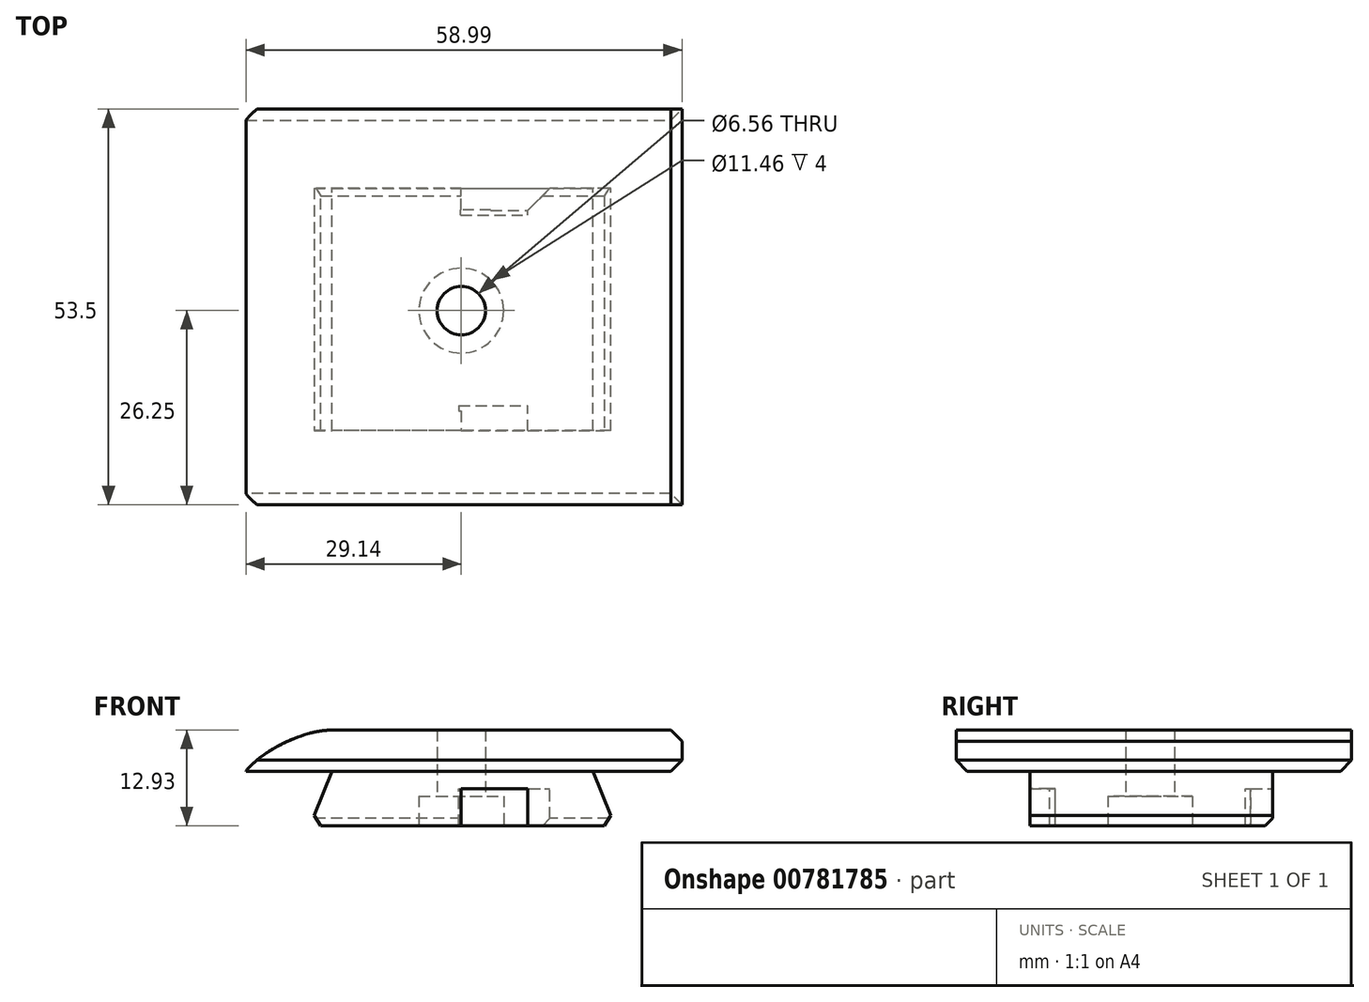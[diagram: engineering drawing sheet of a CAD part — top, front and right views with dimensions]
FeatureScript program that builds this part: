
annotation { "Feature Type Name" : "Feature", "Feature Type Description" : "" }
export const myFeature = defineFeature(function(context is Context, id is Id, definition is map)
    precondition{}
    {
        {
            var Q0;
            Q0=qCreatedBy(makeId("Front.planeOp"),FACE);
            var sketch = newSketch(context, id + "F0", { "sketchPlane" : qUnion([Q0])});
            skLineSegment(sketch, "E0", {"start": v(-49.44, 13.06) * mm, "end": v(-14.15, 13.06) * mm});
            skLineSegment(sketch, "E1", {"start": v(-14.15, 5.69) * mm, "end": v(-11.15, 5.69) * mm});
            skLineSegment(sketch, "E2", {"start": v(-11.15, 5.69) * mm, "end": v(-14.15, 13.06) * mm});
            skLineSegment(sketch, "E3", {"start": v(-49.44, 5.69) * mm, "end": v(-52.44, 5.69) * mm});
            skLineSegment(sketch, "E4", {"start": v(-52.44, 5.69) * mm, "end": v(-49.44, 13.06) * mm});
            skLineSegment(sketch, "E5", {"start": v(-49.44, 5.69) * mm, "end": v(-27.95, 5.69) * mm});
            skLineSegment(sketch, "E6", {"start": v(-27.95, 5.69) * mm, "end": v(-27.95, 10.69) * mm});
            skLineSegment(sketch, "E7", {"start": v(-27.95, 10.69) * mm, "end": v(-22.95, 10.69) * mm});
            skLineSegment(sketch, "E8", {"start": v(-22.95, 10.69) * mm, "end": v(-22.95, 5.69) * mm});
            skLineSegment(sketch, "E9", {"start": v(-22.95, 5.69) * mm, "end": v(-14.15, 5.69) * mm});
            skSolve(sketch);
        }
        {
            var Q0;
            Q0=makeQuery(id+"F0.imprint","IMPRINT",FACE,{"disambiguationData":[TD([[makeQuery(id+"F0.imprint","IMPRINT",EDGE,{"derivedFrom":sQuery(id+"F0.wireOp",EDGE,"E0")}),-1.0]])]});
            extrude(context, id + "F1", {"entities" : qUnion([Q0]), "depth" : 33.1 * mm, "offsetDistance" : 25 * mm});
        }
        {
            var Q0;
            Q0=makeQuery(id+"F1.opExtrude","SWEPT_FACE",FACE,{"disambiguationData":[OSD([sQuery(id+"F0.wireOp",EDGE,"E3"),sQuery(id+"F0.wireOp",EDGE,"E5")])]});
            var sketch = newSketch(context, id + "F2", { "sketchPlane" : qUnion([Q0])});
            skLineSegment(sketch, "E10", {"start": v(-27.95, 30.12) * mm, "end": v(-22.95, 30.12) * mm});
            skLineSegment(sketch, "E11", {"start": v(-27.95, 30.12) * mm, "end": v(-27.95, 2.97) * mm});
            skLineSegment(sketch, "E12", {"start": v(-27.95, 2.97) * mm, "end": v(-22.95, 2.97) * mm});
            skLineSegment(sketch, "E13", {"start": v(-22.95, 30.12) * mm, "end": v(-22.95, 2.97) * mm});
            skSolve(sketch);
        }
        {
            var Q0;
            Q0=makeQuery(id+"F2.imprint","IMPRINT",FACE,{"disambiguationData":[TD([[makeQuery(id+"F2.imprint","IMPRINT",EDGE,{"derivedFrom":sQuery(id+"F2.wireOp",EDGE,"E10")}),-1.0]])]});
            extrude(context, id + "F3", {"entities" : qUnion([Q0]), "oppositeDirection" : true, "depth" : 5 * mm, "offsetDistance" : 25 * mm});
        }
        {
            var Q0;
            Q0=makeQuery(id+"F1.opExtrude","SWEPT_FACE",FACE,{"disambiguationData":[OSD([sQuery(id+"F0.wireOp",EDGE,"E0")])]});
            var sketch = newSketch(context, id + "F4", { "sketchPlane" : qUnion([Q0])});
            skLineSegment(sketch, "E14", {"start": v(-49.44, -16.55) * mm, "end": v(-49.44, -33.1) * mm});
            skCircle(sketch, "E15", {"center": v(-31.95, -16.55) * mm, "radius": 5 * mm});
            skPoint(sketch, "E16.orphan", {"position": v(-31.95, 0) * mm});
            skPoint(sketch, "E17.orphan", {"position": v(-49.44, 0) * mm});
            skPoint(sketch, "E18.end.orphan", {"position": v(-31.95, -33.1) * mm});
            skSolve(sketch);
        }
        {
            var Q0;
            Q0=makeQuery(id+"F4.imprint","IMPRINT",FACE,{"disambiguationData":[TD([[makeQuery(id+"F4.imprint","IMPRINT",EDGE,{"derivedFrom":sQuery(id+"F4.wireOp",EDGE,"E15")}),1.0]])]});
            extrude(context, id + "F5", {"entities" : qUnion([Q0]), "operationType" : NewBodyOperationType.REMOVE, "oppositeDirection" : true, "depth" : 25 * mm, "offsetDistance" : 25 * mm});
        }
        {
            var Q0;
            Q0=makeQuery(id+"F3.opExtrude","CAP_FACE",FACE,{"disambiguationData":[OSD([sQuery(id+"F2.wireOp",EDGE,"E10"),sQuery(id+"F2.wireOp",EDGE,"E11"),sQuery(id+"F2.wireOp",EDGE,"E12"),sQuery(id+"F2.wireOp",EDGE,"E13")])],"isStart":true});
            var sketch = newSketch(context, id + "F6", { "sketchPlane" : qUnion([Q0])});
            skArc(sketch, "E19", {"start": v(-27.95, 13.55) * mm, "mid": v(-26.95, 16.55) * mm, "end": v(-27.95, 19.55) * mm});
            skLineSegment(sketch, "E20", {"start": v(-27.95, 19.55) * mm, "end": v(-27.95, 13.55) * mm});
            skSolve(sketch);
        }
        {
            var Q0;
            Q0=makeQuery(id+"F6.imprint","IMPRINT",FACE,{"disambiguationData":[TD([[makeQuery(id+"F6.imprint","IMPRINT",EDGE,{"derivedFrom":sQuery(id+"F6.wireOp",EDGE,"E19")}),1.0]])]});
            extrude(context, id + "F7", {"entities" : qUnion([Q0]), "operationType" : NewBodyOperationType.REMOVE, "oppositeDirection" : true, "depth" : 25 * mm, "offsetDistance" : 25 * mm});
        }
        {
            var Q0;
            Q0=makeQuery(id+"F1.opExtrude","CAP_FACE",FACE,{"disambiguationData":[OSD([sQuery(id+"F0.wireOp",EDGE,"E0"),sQuery(id+"F0.wireOp",EDGE,"E1"),sQuery(id+"F0.wireOp",EDGE,"E2"),sQuery(id+"F0.wireOp",EDGE,"E3"),sQuery(id+"F0.wireOp",EDGE,"E4"),sQuery(id+"F0.wireOp",EDGE,"E5"),sQuery(id+"F0.wireOp",EDGE,"E6"),sQuery(id+"F0.wireOp",EDGE,"E7"),sQuery(id+"F0.wireOp",EDGE,"E8"),sQuery(id+"F0.wireOp",EDGE,"E9")])],"isStart":false});
            var sketch = newSketch(context, id + "F8", { "sketchPlane" : qUnion([Q0])});
            skLineSegment(sketch, "E21", {"start": v(-52.44, 5.69) * mm, "end": v(-27.95, 5.69) * mm});
            skLineSegment(sketch, "E22", {"start": v(-27.95, 5.69) * mm, "end": v(-27.95, 10.69) * mm});
            skLineSegment(sketch, "E23", {"start": v(-27.95, 10.69) * mm, "end": v(-22.95, 10.69) * mm});
            skLineSegment(sketch, "E24", {"start": v(-22.95, 10.69) * mm, "end": v(-22.95, 5.69) * mm});
            skLineSegment(sketch, "E25", {"start": v(-22.95, 5.69) * mm, "end": v(-11.15, 5.69) * mm});
            skLineSegment(sketch, "E26", {"start": v(-11.15, 5.69) * mm, "end": v(-14.15, 13.06) * mm});
            skLineSegment(sketch, "E27", {"start": v(-14.15, 13.06) * mm, "end": v(-49.44, 13.06) * mm});
            skLineSegment(sketch, "E28", {"start": v(-49.44, 13.06) * mm, "end": v(-52.44, 5.69) * mm});
            skSolve(sketch);
        }
        {
            var Q0;
            Q0=makeQuery(id+"F8.imprint","IMPRINT",FACE,{"disambiguationData":[TD([[makeQuery(id+"F8.imprint","IMPRINT",EDGE,{"derivedFrom":sQuery(id+"F8.wireOp",EDGE,"E21")}),-1.0]])]});
            extrude(context, id + "F9", {"entities" : qUnion([Q0]), "operationType" : NewBodyOperationType.REMOVE, "oppositeDirection" : true, "depth" : .3 * mm, "offsetDistance" : 25 * mm});
        }
        {
            var Q0;
            Q0=makeQuery(id+"F9.boolean.opBoolean","COPY",FACE,{"derivedFrom":makeQuery(id+"F9.opExtrude","CAP_FACE",FACE,{"disambiguationData":[OSD([sQuery(id+"F8.wireOp",EDGE,"E21"),sQuery(id+"F8.wireOp",EDGE,"E22"),sQuery(id+"F8.wireOp",EDGE,"E23"),sQuery(id+"F8.wireOp",EDGE,"E24"),sQuery(id+"F8.wireOp",EDGE,"E25"),sQuery(id+"F8.wireOp",EDGE,"E26"),sQuery(id+"F8.wireOp",EDGE,"E27"),sQuery(id+"F8.wireOp",EDGE,"E28")])],"isStart":false})});
            var sketch = newSketch(context, id + "F10", { "sketchPlane" : qUnion([Q0])});
            skLineSegment(sketch, "E29.bottom", {"start": v(-31.95, 5.69) * mm, "end": v(-22.95, 5.69) * mm});
            skLineSegment(sketch, "E29.top", {"start": v(-31.95, 10.69) * mm, "end": v(-22.95, 10.69) * mm});
            skLineSegment(sketch, "E29.left", {"start": v(-31.95, 5.69) * mm, "end": v(-31.95, 10.69) * mm});
            skLineSegment(sketch, "E29.right", {"start": v(-22.95, 5.69) * mm, "end": v(-22.95, 10.69) * mm});
            skSolve(sketch);
        }
        {
            var Q0;
            {var subQ2=sQuery(id+"F10.wireOp",EDGE,"E29.left");Q0=makeQuery(id+"F10.imprint","IMPRINT",FACE,{"disambiguationData":[TD([[makeQuery(id+"F10.imprint","IMPRINT",EDGE,{"derivedFrom":subQ2}),-1.0]])]});}
            extrude(context, id + "F11", {"entities" : qUnion([Q0]), "operationType" : NewBodyOperationType.REMOVE, "oppositeDirection" : true, "depth" : 2.66 * mm, "offsetDistance" : 25 * mm});
        }
        {
            var Q0;
            Q0=makeQuery(id+"F1.opExtrude","CAP_FACE",FACE,{"disambiguationData":[OSD([sQuery(id+"F0.wireOp",EDGE,"E0"),sQuery(id+"F0.wireOp",EDGE,"E1"),sQuery(id+"F0.wireOp",EDGE,"E2"),sQuery(id+"F0.wireOp",EDGE,"E3"),sQuery(id+"F0.wireOp",EDGE,"E4"),sQuery(id+"F0.wireOp",EDGE,"E5"),sQuery(id+"F0.wireOp",EDGE,"E6"),sQuery(id+"F0.wireOp",EDGE,"E7"),sQuery(id+"F0.wireOp",EDGE,"E8"),sQuery(id+"F0.wireOp",EDGE,"E9")])],"isStart":true});
            var sketch = newSketch(context, id + "F12", { "sketchPlane" : qUnion([Q0])});
            skLineSegment(sketch, "E30.bottom", {"start": v(22.95, 5.69) * mm, "end": v(31.95, 5.69) * mm});
            skLineSegment(sketch, "E30.top", {"start": v(22.95, 10.69) * mm, "end": v(31.95, 10.69) * mm});
            skLineSegment(sketch, "E30.left", {"start": v(22.95, 5.69) * mm, "end": v(22.95, 10.69) * mm});
            skLineSegment(sketch, "E30.right", {"start": v(31.95, 5.69) * mm, "end": v(31.95, 10.69) * mm});
            skSolve(sketch);
        }
        {
            var Q0;
            {var subQ2=sQuery(id+"F12.wireOp",EDGE,"E30.right");Q0=makeQuery(id+"F12.imprint","IMPRINT",FACE,{"disambiguationData":[TD([[makeQuery(id+"F12.imprint","IMPRINT",EDGE,{"derivedFrom":subQ2}),1.0]])]});}
            extrude(context, id + "F13", {"entities" : qUnion([Q0]), "operationType" : NewBodyOperationType.REMOVE, "oppositeDirection" : true, "depth" : 2.91 * mm, "offsetDistance" : 25 * mm});
        }
        {
            var Q0;
            Q0=makeQuery(id+"F1.opExtrude","SWEPT_EDGE",EDGE,{"disambiguationData":[OSD([sQuery(id+"F0.wireOp",EDGE,"E1"),sQuery(id+"F0.wireOp",EDGE,"E2")])]});
            var Q1;
            Q1=makeQuery(id+"F1.opExtrude","CAP_EDGE",EDGE,{"disambiguationData":[OSD([sQuery(id+"F0.wireOp",EDGE,"E1"),sQuery(id+"F0.wireOp",EDGE,"E9")])],"isStart":true});
            var Q2;
            Q2=makeQuery(id+"F1.opExtrude","CAP_EDGE",EDGE,{"disambiguationData":[OSD([sQuery(id+"F0.wireOp",EDGE,"E3"),sQuery(id+"F0.wireOp",EDGE,"E5")])],"isStart":true});
            var Q3;
            Q3=makeQuery(id+"F1.opExtrude","SWEPT_EDGE",EDGE,{"disambiguationData":[OSD([sQuery(id+"F0.wireOp",EDGE,"E3"),sQuery(id+"F0.wireOp",EDGE,"E4")])]});
            var Q4;
            Q4=makeQuery(id+"F9.boolean.opBoolean","COPY",EDGE,{"derivedFrom":makeQuery(id+"F9.opExtrude","CAP_EDGE",EDGE,{"disambiguationData":[OSD([sQuery(id+"F8.wireOp",EDGE,"E21")])],"isStart":false})});
            var Q5;
            Q5=makeQuery(id+"F9.boolean.opBoolean","COPY",EDGE,{"derivedFrom":makeQuery(id+"F9.opExtrude","CAP_EDGE",EDGE,{"disambiguationData":[OSD([sQuery(id+"F8.wireOp",EDGE,"E25")])],"isStart":false})});
            chamfer(context, id + "F14", {"entities" : qUnion([Q0, Q1, Q2, Q3, Q4, Q5]), "width" : 1 * mm, "tangentPropagation" : true});
        }
        {
            var Q0;
            Q0=makeQuery(id+"F11.boolean.opBoolean","COPY",EDGE,{"derivedFrom":makeQuery(id+"F11.opExtrude","CAP_EDGE",EDGE,{"disambiguationData":[OSD([sQuery(id+"F10.wireOp",EDGE,"E29.left")])],"isStart":true})});
            var Q1;
            Q1=makeQuery(id+"F9.boolean.opBoolean","COPY",EDGE,{"derivedFrom":makeQuery(id+"F9.opExtrude","CAP_EDGE",EDGE,{"disambiguationData":[OSD([sQuery(id+"F8.wireOp",EDGE,"E24")])],"isStart":false})});
            var Q2;
            Q2=makeQuery(id+"F13.boolean.opBoolean","COPY",EDGE,{"derivedFrom":makeQuery(id+"F13.opExtrude","CAP_EDGE",EDGE,{"disambiguationData":[OSD([sQuery(id+"F12.wireOp",EDGE,"E30.right")])],"isStart":true})});
            var Q3;
            Q3=makeQuery(id+"F1.opExtrude","CAP_EDGE",EDGE,{"disambiguationData":[OSD([sQuery(id+"F0.wireOp",EDGE,"E8")])],"isStart":true});
            chamfer(context, id + "F15", {"entities" : qUnion([Q0, Q1, Q2, Q3]), "width" : 3 * mm, "tangentPropagation" : true});
        }
        {
            var Q0;
            Q0=makeQuery(id+"F11.boolean.opBoolean","COPY",FACE,{"derivedFrom":makeQuery(id+"F11.opExtrude","CAP_FACE",FACE,{"disambiguationData":[OSD([sQuery(id+"F8.wireOp",EDGE,"E22"),sQuery(id+"F10.wireOp",EDGE,"E29.bottom"),sQuery(id+"F10.wireOp",EDGE,"E29.top"),sQuery(id+"F10.wireOp",EDGE,"E29.left")])],"isStart":false})});
            var sketch = newSketch(context, id + "F16", { "sketchPlane" : qUnion([Q0])});
            skLineSegment(sketch, "E31.bottom", {"start": v(-32.3, 5.69) * mm, "end": v(-22.96, 5.69) * mm});
            skLineSegment(sketch, "E31.top", {"start": v(-32.3, 10.69) * mm, "end": v(-22.96, 10.69) * mm});
            skLineSegment(sketch, "E31.left", {"start": v(-32.3, 5.69) * mm, "end": v(-32.3, 10.69) * mm});
            skLineSegment(sketch, "E31.right", {"start": v(-22.96, 5.69) * mm, "end": v(-22.96, 10.69) * mm});
            skSolve(sketch);
        }
        {
            var Q0;
            Q0 = qSketchRegion(id + "F16", true);
            extrude(context, id + "F17", {"entities" : qUnion([Q0]), "operationType" : NewBodyOperationType.REMOVE, "oppositeDirection" : true, "depth" : .75 * mm, "offsetDistance" : 25 * mm});
        }
        {
            var Q0;
            Q0=makeQuery(id+"F1.opExtrude","SWEPT_BODY",BODY,{"disambiguationData":[OSD([sQuery(id+"F0.wireOp",EDGE,"E0"),sQuery(id+"F0.wireOp",EDGE,"E1"),sQuery(id+"F0.wireOp",EDGE,"E2"),sQuery(id+"F0.wireOp",EDGE,"E3"),sQuery(id+"F0.wireOp",EDGE,"E4"),sQuery(id+"F0.wireOp",EDGE,"E5"),sQuery(id+"F0.wireOp",EDGE,"E6"),sQuery(id+"F0.wireOp",EDGE,"E7"),sQuery(id+"F0.wireOp",EDGE,"E8"),sQuery(id+"F0.wireOp",EDGE,"E9")])]});
            var Q1;
            Q1=makeQuery(id+"F3.opExtrude","SWEPT_BODY",BODY,{"disambiguationData":[OSD([sQuery(id+"F2.wireOp",EDGE,"E10"),sQuery(id+"F2.wireOp",EDGE,"E11"),sQuery(id+"F2.wireOp",EDGE,"E12"),sQuery(id+"F2.wireOp",EDGE,"E13")])]});
            booleanBodies(context, id + "F18", {"operationType" : BooleanOperationType.UNION, "tools" : qUnion([Q0, Q1])});
        }
        {
            var Q0;
            Q0=makeQuery(id+"F3.opExtrude","SWEPT_FACE",FACE,{"disambiguationData":[OSD([sQuery(id+"F2.wireOp",EDGE,"E10")])]});
            var sketch = newSketch(context, id + "F19", { "sketchPlane" : qUnion([Q0])});
            skLineSegment(sketch, "E32.bottom", {"start": v(-27.95, 5.69) * mm, "end": v(-22.95, 5.69) * mm});
            skLineSegment(sketch, "E32.top", {"start": v(-27.95, 10.69) * mm, "end": v(-22.95, 10.69) * mm});
            skLineSegment(sketch, "E32.left", {"start": v(-27.95, 5.69) * mm, "end": v(-27.95, 10.69) * mm});
            skLineSegment(sketch, "E32.right", {"start": v(-22.95, 5.69) * mm, "end": v(-22.95, 10.69) * mm});
            skSolve(sketch);
        }
        {
            var Q0;
            Q0 = qSketchRegion(id + "F19", true);
            extrude(context, id + "F20", {"entities" : qUnion([Q0]), "operationType" : NewBodyOperationType.REMOVE, "oppositeDirection" : true, "depth" : .7 * mm, "offsetDistance" : 25 * mm});
        }
        {
            var Q0;
            Q0=makeQuery(id+"F13.boolean.opBoolean","COPY",FACE,{"derivedFrom":makeQuery(id+"F13.opExtrude","CAP_FACE",FACE,{"disambiguationData":[OSD([sQuery(id+"F0.wireOp",EDGE,"E6"),sQuery(id+"F12.wireOp",EDGE,"E30.bottom"),sQuery(id+"F12.wireOp",EDGE,"E30.top"),sQuery(id+"F12.wireOp",EDGE,"E30.right")])],"isStart":false})});
            var sketch = newSketch(context, id + "F21", { "sketchPlane" : qUnion([Q0])});
            skLineSegment(sketch, "E33.bottom", {"start": v(32.04, 5.69) * mm, "end": v(22.95, 5.69) * mm});
            skLineSegment(sketch, "E33.top", {"start": v(32.04, 10.66) * mm, "end": v(22.95, 10.66) * mm});
            skLineSegment(sketch, "E33.left", {"start": v(32.04, 5.69) * mm, "end": v(32.04, 10.66) * mm});
            skLineSegment(sketch, "E33.right", {"start": v(22.95, 5.69) * mm, "end": v(22.95, 10.66) * mm});
            skSolve(sketch);
        }
        {
            var Q0;
            Q0 = qSketchRegion(id + "F21", true);
            extrude(context, id + "F22", {"entities" : qUnion([Q0]), "operationType" : NewBodyOperationType.REMOVE, "oppositeDirection" : true, "depth" : .75 * mm, "offsetDistance" : 25 * mm});
        }
        {
            var Q0;
            Q0=makeQuery(id+"F9.boolean.opBoolean","COPY",FACE,{"derivedFrom":makeQuery(id+"F9.opExtrude","CAP_FACE",FACE,{"disambiguationData":[OSD([sQuery(id+"F8.wireOp",EDGE,"E21"),sQuery(id+"F8.wireOp",EDGE,"E22"),sQuery(id+"F8.wireOp",EDGE,"E23"),sQuery(id+"F8.wireOp",EDGE,"E24"),sQuery(id+"F8.wireOp",EDGE,"E25"),sQuery(id+"F8.wireOp",EDGE,"E26"),sQuery(id+"F8.wireOp",EDGE,"E27"),sQuery(id+"F8.wireOp",EDGE,"E28")])],"isStart":false})});
            var sketch = newSketch(context, id + "F23", { "sketchPlane" : qUnion([Q0])});
            skLineSegment(sketch, "E34", {"start": v(-49.44, 13.06) * mm, "end": v(-61.09, 13.06) * mm});
            skLineSegment(sketch, "E35", {"start": v(-61.09, 13.06) * mm, "end": v(-61.09, 18.62) * mm});
            skLineSegment(sketch, "E36", {"start": v(-14.15, 13.06) * mm, "end": v(-2.1, 13.06) * mm});
            skLineSegment(sketch, "E37", {"start": v(-2.1, 13.06) * mm, "end": v(-2.1, 18.62) * mm});
            skLineSegment(sketch, "E38", {"start": v(-2.1, 18.62) * mm, "end": v(-61.09, 18.62) * mm});
            skSolve(sketch);
        }
        {
            var Q0;
            Q0=makeQuery(id+"F23.imprint","IMPRINT",FACE,{"disambiguationData":[TD([[makeQuery(id+"F23.imprint","IMPRINT",EDGE,{"derivedFrom":sQuery(id+"F23.wireOp",EDGE,"E34")}),-1.0]])]});
            extrude(context, id + "F24", {"entities" : qUnion([Q0]), "operationType" : NewBodyOperationType.ADD, "oppositeDirection" : true, "depth" : 43.5 * mm, "offsetDistance" : 25 * mm});
        }
        {
            var Q0;
            {var subQ0=sQuery(id+"F8.wireOp",EDGE,"E27");Q0=makeQuery(id+"F24.boolean.opBoolean","MERGE",FACE,{"derivedFrom":[makeQuery(id+"F9.boolean.opBoolean","COPY",FACE,{"derivedFrom":makeQuery(id+"F9.opExtrude","CAP_FACE",FACE,{"disambiguationData":[OSD([sQuery(id+"F8.wireOp",EDGE,"E21"),sQuery(id+"F8.wireOp",EDGE,"E22"),sQuery(id+"F8.wireOp",EDGE,"E23"),sQuery(id+"F8.wireOp",EDGE,"E24"),sQuery(id+"F8.wireOp",EDGE,"E25"),sQuery(id+"F8.wireOp",EDGE,"E26"),subQ0,sQuery(id+"F8.wireOp",EDGE,"E28")])],"isStart":false})}),makeQuery(id+"F24.opExtrude","CAP_FACE",FACE,{"disambiguationData":[OSD([subQ0,sQuery(id+"F23.wireOp",EDGE,"E34"),sQuery(id+"F23.wireOp",EDGE,"E35"),sQuery(id+"F23.wireOp",EDGE,"E36"),sQuery(id+"F23.wireOp",EDGE,"E37"),sQuery(id+"F23.wireOp",EDGE,"E38")])],"isStart":true})]});}
            var sketch = newSketch(context, id + "F25", { "sketchPlane" : qUnion([Q0])});
            skLineSegment(sketch, "E39.bottom", {"start": v(-61.09, 18.62) * mm, "end": v(-2.1, 18.62) * mm});
            skLineSegment(sketch, "E39.top", {"start": v(-61.09, 13.06) * mm, "end": v(-2.1, 13.06) * mm});
            skLineSegment(sketch, "E39.left", {"start": v(-61.09, 18.62) * mm, "end": v(-61.09, 13.06) * mm});
            skLineSegment(sketch, "E39.right", {"start": v(-2.1, 18.62) * mm, "end": v(-2.1, 13.06) * mm});
            skSolve(sketch);
        }
        {
            var Q0;
            Q0=makeQuery(id+"F25.imprint","IMPRINT",FACE,{"disambiguationData":[TD([[makeQuery(id+"F25.imprint","IMPRINT",EDGE,{"derivedFrom":sQuery(id+"F25.wireOp",EDGE,"E39.bottom")}),1.0]])]});
            extrude(context, id + "F26", {"entities" : qUnion([Q0]), "operationType" : NewBodyOperationType.ADD, "depth" : 10 * mm, "offsetDistance" : 25 * mm});
        }
        {
            var Q0;
            Q0=makeQuery(id+"F24.boolean.opBoolean","SPLIT",FACE,{"disambiguationData":[TD([makeQuery(id+"F5.boolean.opBoolean","COPY",FACE,{"derivedFrom":makeQuery(id+"F5.opExtrude","SWEPT_FACE",FACE,{"disambiguationData":[OSD([sQuery(id+"F4.wireOp",EDGE,"E15")])]})})])],"derivedFrom":makeQuery(id+"F24.opExtrude","SWEPT_FACE",FACE,{"disambiguationData":[OSD([sQuery(id+"F8.wireOp",EDGE,"E27"),sQuery(id+"F23.wireOp",EDGE,"E34"),sQuery(id+"F23.wireOp",EDGE,"E36")])]})});
            var sketch = newSketch(context, id + "F27", { "sketchPlane" : qUnion([Q0])});
            skCircle(sketch, "E40", {"center": v(-31.95, 16.55) * mm, "radius": 5 * mm});
            skPoint(sketch, "E40.first.point", {"position": v(-35.68, 19.88) * mm});
            skPoint(sketch, "E40.second.point", {"position": v(-28.24, 13.2) * mm});
            skPoint(sketch, "E40.third.point", {"position": v(-27.95, 19.55) * mm});
            skCircle(sketch, "E41", {"center": v(-31.95, 16.55) * mm, "radius": 3.28 * mm});
            skSolve(sketch);
        }
        {
            var Q0;
            Q0=makeQuery(id+"F27.imprint","IMPRINT",FACE,{"disambiguationData":[TD([[makeQuery(id+"F27.imprint","IMPRINT",EDGE,{"derivedFrom":sQuery(id+"F27.wireOp",EDGE,"E41")}),1.0]])]});
            extrude(context, id + "F28", {"entities" : qUnion([Q0]), "operationType" : NewBodyOperationType.REMOVE, "oppositeDirection" : true, "depth" : 25 * mm, "offsetDistance" : 25 * mm});
        }
        {
            var Q0;
            Q0=makeQuery(id+"F24.boolean.opBoolean","SPLIT",FACE,{"disambiguationData":[TD([makeQuery(id+"F5.boolean.opBoolean","COPY",FACE,{"derivedFrom":makeQuery(id+"F5.opExtrude","SWEPT_FACE",FACE,{"disambiguationData":[OSD([sQuery(id+"F4.wireOp",EDGE,"E15")])]})})])],"derivedFrom":makeQuery(id+"F24.opExtrude","SWEPT_FACE",FACE,{"disambiguationData":[OSD([sQuery(id+"F8.wireOp",EDGE,"E27"),sQuery(id+"F23.wireOp",EDGE,"E34"),sQuery(id+"F23.wireOp",EDGE,"E36")])]})});
            extrude(context, id + "F29", {"entities" : qUnion([Q0]), "operationType" : NewBodyOperationType.ADD, "depth" : 7.37 * mm, "offsetDistance" : 25 * mm});
        }
        {
            var Q0;
            Q0=makeQuery(id+"F29.boolean.opBoolean","MERGE",FACE,{"derivedFrom":[makeQuery(id+"F18.opBoolean","MERGE",FACE,{"derivedFrom":[makeQuery(id+"F3.opExtrude","CAP_FACE",FACE,{"disambiguationData":[OSD([sQuery(id+"F2.wireOp",EDGE,"E10"),sQuery(id+"F2.wireOp",EDGE,"E11"),sQuery(id+"F2.wireOp",EDGE,"E12"),sQuery(id+"F2.wireOp",EDGE,"E13")])],"isStart":true}),makeQuery(id+"F1.opExtrude","SWEPT_FACE",FACE,{"disambiguationData":[OSD([sQuery(id+"F0.wireOp",EDGE,"E1"),sQuery(id+"F0.wireOp",EDGE,"E9")])]}),makeQuery(id+"F1.opExtrude","SWEPT_FACE",FACE,{"disambiguationData":[OSD([sQuery(id+"F0.wireOp",EDGE,"E3"),sQuery(id+"F0.wireOp",EDGE,"E5")])]})]}),makeQuery(id+"F29.opExtrude","CAP_FACE",FACE,{"disambiguationData":[OSD([sQuery(id+"F8.wireOp",EDGE,"E27"),sQuery(id+"F23.wireOp",EDGE,"E34"),sQuery(id+"F23.wireOp",EDGE,"E36")])],"isStart":false})]});
            var sketch = newSketch(context, id + "F30", { "sketchPlane" : qUnion([Q0])});
            skCircle(sketch, "E42", {"center": v(-31.95, 16.55) * mm, "radius": 3.28 * mm});
            skPoint(sketch, "E42.first.point", {"position": v(-34.28, 18.85) * mm});
            skPoint(sketch, "E42.second.point", {"position": v(-28.68, 16.62) * mm});
            skPoint(sketch, "E42.third.point", {"position": v(-32.98, 13.44) * mm});
            skCircle(sketch, "E43", {"center": v(-31.95, 16.55) * mm, "radius": 5.73 * mm});
            skSolve(sketch);
        }
        {
            var Q0;
            Q0=makeQuery(id+"F30.imprint","IMPRINT",FACE,{"disambiguationData":[TD([[makeQuery(id+"F30.imprint","IMPRINT",EDGE,{"derivedFrom":sQuery(id+"F30.wireOp",EDGE,"E42")}),-1.0]])]});
            extrude(context, id + "F31", {"entities" : qUnion([Q0]), "operationType" : NewBodyOperationType.REMOVE, "oppositeDirection" : true, "depth" : 4 * mm, "offsetDistance" : 25 * mm});
        }
        {
            var Q0;
            Q0=makeQuery(id+"F26.boolean.opBoolean","MERGE",EDGE,{"derivedFrom":[makeQuery(id+"F24.opExtrude","SWEPT_EDGE",EDGE,{"disambiguationData":[OSD([sQuery(id+"F23.wireOp",EDGE,"E35"),sQuery(id+"F23.wireOp",EDGE,"E38")])]}),makeQuery(id+"F26.opExtrude","SWEPT_EDGE",EDGE,{"disambiguationData":[OSD([sQuery(id+"F25.wireOp",EDGE,"E39.bottom"),sQuery(id+"F25.wireOp",EDGE,"E39.left")])]})]});
            fillet(context, id + "F32", {"entities" : qUnion([Q0]), "radius" : 15 * mm, "rho" : .4, "crossSection" : FilletCrossSection.CONIC, "allowEdgeOverflow" : false});
        }
        {
            var Q0;
            Q0=makeQuery(id+"F24.opExtrude","CAP_EDGE",EDGE,{"disambiguationData":[OSD([sQuery(id+"F8.wireOp",EDGE,"E27"),sQuery(id+"F23.wireOp",EDGE,"E34"),sQuery(id+"F23.wireOp",EDGE,"E36")])],"isStart":false});
            var Q1;
            Q1=makeQuery(id+"F26.boolean.opBoolean","MERGE",EDGE,{"derivedFrom":[makeQuery(id+"F24.opExtrude","SWEPT_EDGE",EDGE,{"disambiguationData":[OSD([sQuery(id+"F23.wireOp",EDGE,"E36"),sQuery(id+"F23.wireOp",EDGE,"E37")])]}),makeQuery(id+"F26.opExtrude","SWEPT_EDGE",EDGE,{"disambiguationData":[OSD([sQuery(id+"F25.wireOp",EDGE,"E39.top"),sQuery(id+"F25.wireOp",EDGE,"E39.right")])]})]});
            var Q2;
            Q2=makeQuery(id+"F26.opExtrude","CAP_EDGE",EDGE,{"disambiguationData":[OSD([sQuery(id+"F25.wireOp",EDGE,"E39.top")])],"isStart":false});
            chamfer(context, id + "F33", {"entities" : qUnion([Q0, Q1, Q2]), "width" : 1.5 * mm, "tangentPropagation" : true});
        }
        {
            var Q0;
            Q0=makeQuery(id+"F26.boolean.opBoolean","MERGE",EDGE,{"derivedFrom":[makeQuery(id+"F24.opExtrude","SWEPT_EDGE",EDGE,{"disambiguationData":[OSD([sQuery(id+"F23.wireOp",EDGE,"E37"),sQuery(id+"F23.wireOp",EDGE,"E38")])]}),makeQuery(id+"F26.opExtrude","SWEPT_EDGE",EDGE,{"disambiguationData":[OSD([sQuery(id+"F25.wireOp",EDGE,"E39.bottom"),sQuery(id+"F25.wireOp",EDGE,"E39.right")])]})]});
            chamfer(context, id + "F34", {"entities" : qUnion([Q0]), "width" : 1.5 * mm, "tangentPropagation" : true});
        }
    });
